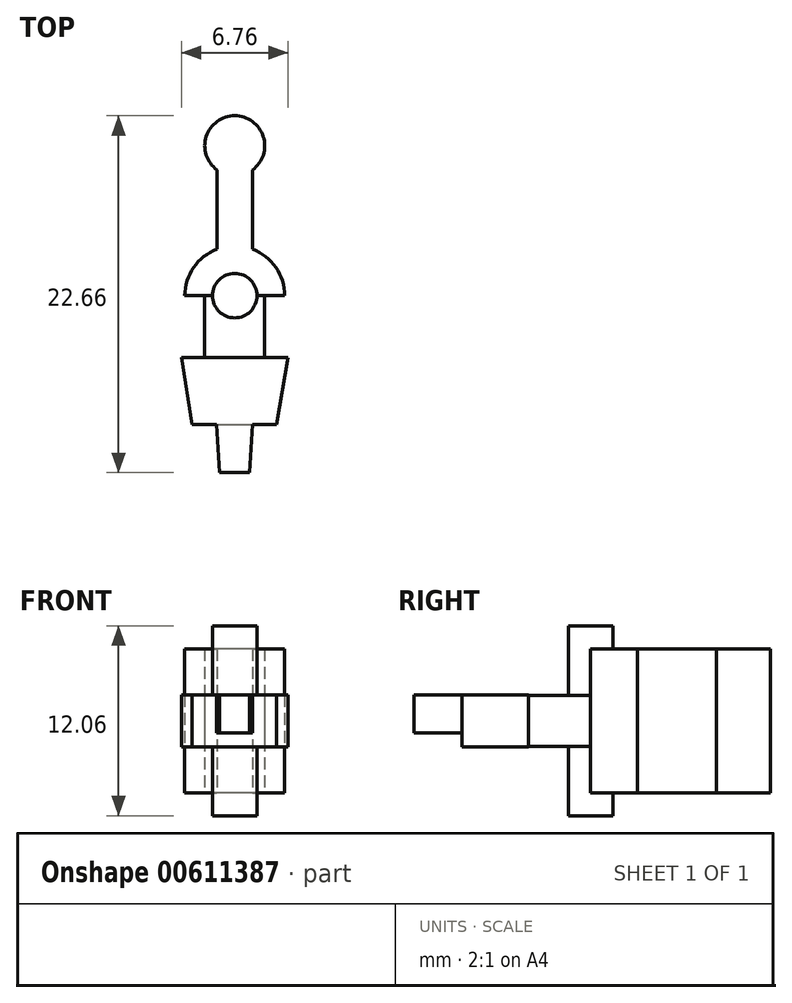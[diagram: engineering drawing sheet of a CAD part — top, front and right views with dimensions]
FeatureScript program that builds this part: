
annotation { "Feature Type Name" : "Feature", "Feature Type Description" : "" }
export const myFeature = defineFeature(function(context is Context, id is Id, definition is map)
    precondition{}
    {
        {
            var Q0;
            Q0=qCreatedBy(makeId("Top.planeOp"),FACE);
            var sketch = newSketch(context, id + "F0", { "sketchPlane" : qUnion([Q0])});
            skLineSegment(sketch, "E0.top", {"start": v(-1.13, -4.71) * mm, "end": v(1.13, -4.71) * mm});
            skLineSegment(sketch, "E0.left", {"start": v(-1.13, 3.28) * mm, "end": v(-1.13, -1.76) * mm});
            skLineSegment(sketch, "E0.right", {"start": v(1.13, 3.28) * mm, "end": v(1.13, -1.76) * mm});
            skArc(sketch, "E1", {"start": v(3.17, -4.71) * mm, "mid": v(2.61, -2.92) * mm, "end": v(1.13, -1.76) * mm});
            skLineSegment(sketch, "E2", {"start": v(-3.17, -4.71) * mm, "end": v(-1.13, -4.71) * mm});
            skArc(sketch, "E3", {"start": v(1.13, 3.28) * mm, "mid": v(0, 6.72) * mm, "end": v(-1.13, 3.28) * mm});
            skArc(sketch, "E4.trimOffspring", {"start": v(-1.13, -1.76) * mm, "mid": v(-2.61, -2.92) * mm, "end": v(-3.17, -4.71) * mm});
            skLineSegment(sketch, "E5.trimOffspring", {"start": v(1.13, -4.71) * mm, "end": v(3.17, -4.71) * mm});
            skSolve(sketch);
        }
        {
            var Q0;
            Q0=makeQuery(id+"F0.imprint","IMPRINT",FACE,{"disambiguationData":[TD([[makeQuery(id+"F0.imprint","IMPRINT",EDGE,{"derivedFrom":sQuery(id+"F0.wireOp",EDGE,"E0.top")}),1.0]])]});
            extrude(context, id + "F1", {"entities" : qUnion([Q0]), "endBound" : BoundingType.SYMMETRIC, "depth" : 9.14 * mm, "offsetDistance" : 25.4 * mm});
        }
        {
            var Q0;
            Q0=qCreatedBy(makeId("Top.planeOp"),FACE);
            var sketch = newSketch(context, id + "F2", { "sketchPlane" : qUnion([Q0])});
            skCircle(sketch, "E6", {"center": v(0, -4.71) * mm, "radius": 1.4 * mm});
            skSolve(sketch);
        }
        {
            var Q0;
            Q0=makeQuery(id+"F2.imprint","IMPRINT",FACE,{"disambiguationData":[TD([[makeQuery(id+"F2.imprint","IMPRINT",EDGE,{"derivedFrom":sQuery(id+"F2.wireOp",EDGE,"E6")}),1.0]])]});
            extrude(context, id + "F3", {"entities" : qUnion([Q0]), "operationType" : NewBodyOperationType.ADD, "endBound" : BoundingType.SYMMETRIC, "depth" : 12.06 * mm, "offsetDistance" : 25.4 * mm});
        }
        {
            var Q0;
            Q0=qCreatedBy(makeId("Top.planeOp"),FACE);
            var sketch = newSketch(context, id + "F4", { "sketchPlane" : qUnion([Q0])});
            skLineSegment(sketch, "E7.bottom", {"start": v(-1.9, -4.71) * mm, "end": v(1.9, -4.71) * mm});
            skLineSegment(sketch, "E7.top", {"start": v(-1.9, -8.65) * mm, "end": v(1.9, -8.65) * mm});
            skLineSegment(sketch, "E7.left", {"start": v(-1.9, -4.71) * mm, "end": v(-1.9, -8.65) * mm});
            skLineSegment(sketch, "E7.right", {"start": v(1.9, -4.71) * mm, "end": v(1.9, -8.65) * mm});
            skSolve(sketch);
        }
        {
            var Q0;
            Q0=makeQuery(id+"F4.imprint","IMPRINT",FACE,{"disambiguationData":[TD([[makeQuery(id+"F4.imprint","IMPRINT",EDGE,{"derivedFrom":sQuery(id+"F4.wireOp",EDGE,"E7.bottom")}),-1.0]])]});
            extrude(context, id + "F5", {"entities" : qUnion([Q0]), "operationType" : NewBodyOperationType.ADD, "endBound" : BoundingType.SYMMETRIC, "depth" : 3.25 * mm, "offsetDistance" : 25.4 * mm});
        }
        {
            var Q0;
            Q0=qCreatedBy(makeId("Top.planeOp"),FACE);
            var sketch = newSketch(context, id + "F6", { "sketchPlane" : qUnion([Q0])});
            skLineSegment(sketch, "E8.bottom", {"start": v(-3.38, -8.65) * mm, "end": v(3.38, -8.65) * mm});
            skLineSegment(sketch, "E8.top", {"start": v(-3.38, -12.9) * mm, "end": v(3.38, -12.9) * mm});
            skLineSegment(sketch, "E8.left", {"start": v(-3.38, -8.65) * mm, "end": v(-3.38, -12.9) * mm});
            skLineSegment(sketch, "E8.right", {"start": v(3.38, -8.65) * mm, "end": v(3.38, -12.9) * mm});
            skLineSegment(sketch, "E9", {"start": v(-3.38, -8.65) * mm, "end": v(-2.7, -12.9) * mm});
            skLineSegment(sketch, "E10", {"start": v(3.38, -8.65) * mm, "end": v(2.66, -12.9) * mm});
            skSolve(sketch);
        }
        {
            var Q0;
            Q0=makeQuery(id+"F6.imprint","IMPRINT",FACE,{"disambiguationData":[TD([[makeQuery(id+"F6.imprint","IMPRINT",EDGE,{"derivedFrom":sQuery(id+"F6.wireOp",EDGE,"E8.bottom")}),-1.0]])]});
            extrude(context, id + "F7", {"entities" : qUnion([Q0]), "operationType" : NewBodyOperationType.ADD, "endBound" : BoundingType.SYMMETRIC, "depth" : 3.3 * mm, "offsetDistance" : 25.4 * mm});
        }
        {
            var Q0;
            Q0=makeQuery(id+"F7.opExtrude","CAP_FACE",FACE,{"disambiguationData":[OSD([sQuery(id+"F6.wireOp",EDGE,"E8.bottom"),sQuery(id+"F6.wireOp",EDGE,"E8.top"),sQuery(id+"F6.wireOp",EDGE,"E9"),sQuery(id+"F6.wireOp",EDGE,"E10")])],"isStart":false});
            var sketch = newSketch(context, id + "F8", { "sketchPlane" : qUnion([Q0])});
            skLineSegment(sketch, "E11.bottom", {"start": v(-1.14, -12.9) * mm, "end": v(1.14, -12.9) * mm});
            skLineSegment(sketch, "E11.top", {"start": v(-1.14, -15.94) * mm, "end": v(1.14, -15.94) * mm});
            skLineSegment(sketch, "E11.left", {"start": v(-1.14, -12.9) * mm, "end": v(-1.14, -15.94) * mm});
            skLineSegment(sketch, "E11.right", {"start": v(1.14, -12.9) * mm, "end": v(1.14, -15.94) * mm});
            skLineSegment(sketch, "E12", {"start": v(-1.14, -12.9) * mm, "end": v(-0.95, -15.94) * mm});
            skLineSegment(sketch, "E13", {"start": v(1.14, -12.9) * mm, "end": v(0.95, -15.94) * mm});
            skLineSegment(sketch, "E14", {"start": v(-0.95, -15.94) * mm, "end": v(0.95, -15.94) * mm});
            skSolve(sketch);
        }
        {
            var Q0;
            Q0=makeQuery(id+"F8.imprint","IMPRINT",FACE,{"disambiguationData":[TD([[makeQuery(id+"F8.imprint","IMPRINT",EDGE,{"derivedFrom":sQuery(id+"F8.wireOp",EDGE,"E11.bottom")}),-1.0]])]});
            extrude(context, id + "F9", {"entities" : qUnion([Q0]), "operationType" : NewBodyOperationType.ADD, "oppositeDirection" : true, "depth" : 2.41 * mm, "offsetDistance" : 25.4 * mm});
        }
    });
